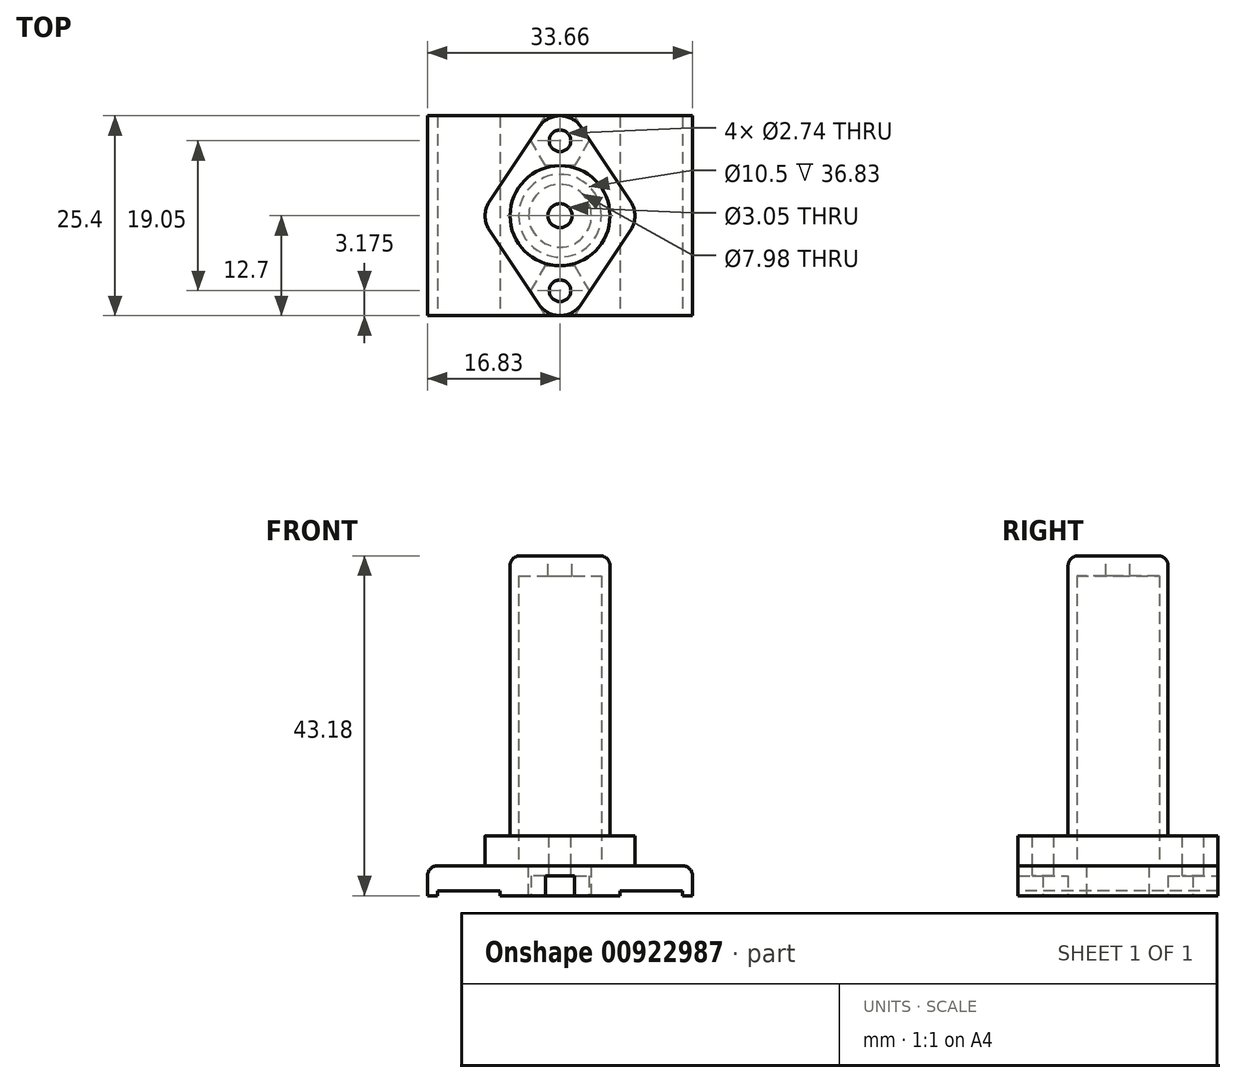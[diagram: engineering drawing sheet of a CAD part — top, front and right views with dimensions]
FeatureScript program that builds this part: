
annotation { "Feature Type Name" : "Feature", "Feature Type Description" : "" }
export const myFeature = defineFeature(function(context is Context, id is Id, definition is map)
    precondition{}
    {
        {
            var Q0;
            Q0=qCreatedBy(makeId("Top.planeOp"),FACE);
            var sketch = newSketch(context, id + "F0", { "sketchPlane" : qUnion([Q0])});
            skCircle(sketch, "E0", {"center": v(0, 0) * mm, "radius": 1.72 * mm});
            skCircle(sketch, "E1", {"center": v(0, 0) * mm, "radius": 2.54 * mm});
            skLineSegment(sketch, "E2", {"start": v(0, -2.54) * mm, "end": v(0, -12.7) * mm});
            skLineSegment(sketch, "E3", {"start": v(2.54, 0) * mm, "end": v(7.62, 0) * mm});
            skLineSegment(sketch, "E4", {"start": v(-2.54, 0) * mm, "end": v(-7.62, 0) * mm});
            skLineSegment(sketch, "E5", {"start": v(-7.62, 0) * mm, "end": v(-15.56, 0) * mm});
            skLineSegment(sketch, "E6", {"start": v(7.62, 0) * mm, "end": v(15.56, 0) * mm});
            skLineSegment(sketch, "E7.bottom", {"start": v(-7.62, 12.7) * mm, "end": v(-15.56, 12.7) * mm});
            skLineSegment(sketch, "E7.top", {"start": v(-7.62, -12.7) * mm, "end": v(-15.56, -12.7) * mm});
            skLineSegment(sketch, "E7.left", {"start": v(-7.62, 12.7) * mm, "end": v(-7.62, -12.7) * mm});
            skLineSegment(sketch, "E7.right", {"start": v(-15.56, 12.7) * mm, "end": v(-15.56, -12.7) * mm});
            skPoint(sketch, "E7.middle", {"position": v(-11.59, 0) * mm});
            skLineSegment(sketch, "E8.bottom", {"start": v(15.56, 12.7) * mm, "end": v(7.62, 12.7) * mm});
            skLineSegment(sketch, "E8.top", {"start": v(15.56, -12.7) * mm, "end": v(7.62, -12.7) * mm});
            skLineSegment(sketch, "E8.left", {"start": v(15.56, 12.7) * mm, "end": v(15.56, -12.7) * mm});
            skLineSegment(sketch, "E8.right", {"start": v(7.62, 12.7) * mm, "end": v(7.62, -12.7) * mm});
            skPoint(sketch, "E8.middle", {"position": v(11.59, 0) * mm});
            skPoint(sketch, "E8.cornerSnap0", {"position": v(-11.59, 12.7) * mm});
            skLineSegment(sketch, "E9.bottom", {"start": v(16.83, -12.7) * mm, "end": v(-16.83, -12.7) * mm});
            skLineSegment(sketch, "E9.top", {"start": v(16.83, 12.7) * mm, "end": v(-16.83, 12.7) * mm});
            skLineSegment(sketch, "E9.left", {"start": v(16.83, -12.7) * mm, "end": v(16.83, 12.7) * mm});
            skLineSegment(sketch, "E9.right", {"start": v(-16.83, -12.7) * mm, "end": v(-16.83, 12.7) * mm});
            skSolve(sketch);
        }
        {
            var Q0;
            {var subQ3=sQuery(id+"F0.wireOp",EDGE,"E9.right");Q0=makeQuery(id+"F0.imprint","IMPRINT",FACE,{"disambiguationData":[TD([[makeQuery(id+"F0.imprint","IMPRINT",EDGE,{"derivedFrom":subQ3}),-1.0]])]});}
            var Q1;
            {var subQ0=sQuery(id+"F0.wireOp",EDGE,"E5");Q1=makeQuery(id+"F0.imprint","IMPRINT",FACE,{"disambiguationData":[TD([[makeQuery(id+"F0.imprint","IMPRINT",EDGE,{"derivedFrom":subQ0}),-1.0]])]});}
            var Q2;
            {var subQ0=sQuery(id+"F0.wireOp",EDGE,"E5");Q2=makeQuery(id+"F0.imprint","IMPRINT",FACE,{"disambiguationData":[TD([[makeQuery(id+"F0.imprint","IMPRINT",EDGE,{"derivedFrom":subQ0}),1.0]])]});}
            var Q3;
            {var subQ4=sQuery(id+"F0.wireOp",EDGE,"E2");Q3=makeQuery(id+"F0.imprint","IMPRINT",FACE,{"disambiguationData":[TD([[makeQuery(id+"F0.imprint","IMPRINT",EDGE,{"derivedFrom":subQ4}),-1.0]])]});}
            var Q4;
            {var subQ4=sQuery(id+"F0.wireOp",EDGE,"E3");Q4=makeQuery(id+"F0.imprint","IMPRINT",FACE,{"disambiguationData":[TD([[makeQuery(id+"F0.imprint","IMPRINT",EDGE,{"derivedFrom":subQ4}),1.0]])]});}
            var Q5;
            {var subQ4=sQuery(id+"F0.wireOp",EDGE,"E2");Q5=makeQuery(id+"F0.imprint","IMPRINT",FACE,{"disambiguationData":[TD([[makeQuery(id+"F0.imprint","IMPRINT",EDGE,{"derivedFrom":subQ4}),1.0]])]});}
            var Q6;
            {var subQ0=sQuery(id+"F0.wireOp",EDGE,"E6");Q6=makeQuery(id+"F0.imprint","IMPRINT",FACE,{"disambiguationData":[TD([[makeQuery(id+"F0.imprint","IMPRINT",EDGE,{"derivedFrom":subQ0}),-1.0]])]});}
            var Q7;
            {var subQ0=sQuery(id+"F0.wireOp",EDGE,"E6");Q7=makeQuery(id+"F0.imprint","IMPRINT",FACE,{"disambiguationData":[TD([[makeQuery(id+"F0.imprint","IMPRINT",EDGE,{"derivedFrom":subQ0}),1.0]])]});}
            var Q8;
            {var subQ3=sQuery(id+"F0.wireOp",EDGE,"E9.left");Q8=makeQuery(id+"F0.imprint","IMPRINT",FACE,{"disambiguationData":[TD([[makeQuery(id+"F0.imprint","IMPRINT",EDGE,{"derivedFrom":subQ3}),1.0]])]});}
            extrude(context, id + "F1", {"entities" : qUnion([Q0, Q1, Q2, Q3, Q4, Q5, Q6, Q7, Q8]), "depth" : 3.8 * mm, "offsetDistance" : 25.4 * mm});
        }
        {
            var Q0;
            {var subQ0=sQuery(id+"F0.wireOp",EDGE,"E5");Q0=makeQuery(id+"F0.imprint","IMPRINT",FACE,{"disambiguationData":[TD([[makeQuery(id+"F0.imprint","IMPRINT",EDGE,{"derivedFrom":subQ0}),1.0]])]});}
            var Q1;
            {var subQ0=sQuery(id+"F0.wireOp",EDGE,"E5");Q1=makeQuery(id+"F0.imprint","IMPRINT",FACE,{"disambiguationData":[TD([[makeQuery(id+"F0.imprint","IMPRINT",EDGE,{"derivedFrom":subQ0}),-1.0]])]});}
            var Q2;
            {var subQ0=sQuery(id+"F0.wireOp",EDGE,"E6");Q2=makeQuery(id+"F0.imprint","IMPRINT",FACE,{"disambiguationData":[TD([[makeQuery(id+"F0.imprint","IMPRINT",EDGE,{"derivedFrom":subQ0}),1.0]])]});}
            var Q3;
            {var subQ0=sQuery(id+"F0.wireOp",EDGE,"E6");Q3=makeQuery(id+"F0.imprint","IMPRINT",FACE,{"disambiguationData":[TD([[makeQuery(id+"F0.imprint","IMPRINT",EDGE,{"derivedFrom":subQ0}),-1.0]])]});}
            extrude(context, id + "F2", {"entities" : qUnion([Q0, Q1, Q2, Q3]), "operationType" : NewBodyOperationType.REMOVE, "depth" : 0.64 * mm, "offsetDistance" : 25.4 * mm});
        }
        {
            var Q0;
            Q0=makeQuery(id+"F1.opExtrude","CAP_FACE",FACE,{"disambiguationData":[OSD([sQuery(id+"F0.wireOp",EDGE,"E1"),sQuery(id+"F0.wireOp",EDGE,"E7.bottom"),sQuery(id+"F0.wireOp",EDGE,"E7.top"),sQuery(id+"F0.wireOp",EDGE,"E8.bottom"),sQuery(id+"F0.wireOp",EDGE,"E8.top"),sQuery(id+"F0.wireOp",EDGE,"E9.bottom"),sQuery(id+"F0.wireOp",EDGE,"E9.top"),sQuery(id+"F0.wireOp",EDGE,"E9.left"),sQuery(id+"F0.wireOp",EDGE,"E9.right")])],"isStart":false});
            var sketch = newSketch(context, id + "F3", { "sketchPlane" : qUnion([Q0])});
            skCircle(sketch, "E10", {"center": v(0, 0) * mm, "radius": 3.99 * mm});
            skSolve(sketch);
        }
        {
            var Q0;
            Q0=makeQuery(id+"F3.imprint","IMPRINT",FACE,{"disambiguationData":[TD([[makeQuery(id+"F3.imprint","IMPRINT",EDGE,{"derivedFrom":sQuery(id+"F3.wireOp",EDGE,"E10")}),1.0]])]});
            extrude(context, id + "F4", {"entities" : qUnion([Q0]), "operationType" : NewBodyOperationType.REMOVE, "endBound" : BoundingType.UP_TO_NEXT, "oppositeDirection" : true, "depth" : 2.08 * mm, "offsetDistance" : 25.4 * mm});
        }
        {
            var Q0;
            Q0=makeQuery(id+"F3.imprint","IMPRINT",FACE,{"disambiguationData":[TD([[makeQuery(id+"F3.imprint","IMPRINT",EDGE,{"derivedFrom":sQuery(id+"F3.wireOp",EDGE,"E10")}),-1.0]])]});
            var sketch = newSketch(context, id + "F5", { "sketchPlane" : qUnion([Q0])});
            skLineSegment(sketch, "E11", {"start": v(0, 0) * mm, "end": v(0, 12.7) * mm});
            skLineSegment(sketch, "E12", {"start": v(0, 0) * mm, "end": v(0, -12.7) * mm});
            skLineSegment(sketch, "E13", {"start": v(0, 12.7) * mm, "end": v(0, 9.52) * mm});
            skLineSegment(sketch, "E14", {"start": v(0, -12.7) * mm, "end": v(0, -9.53) * mm});
            skCircle(sketch, "E15", {"center": v(0, 9.52) * mm, "radius": 1.37 * mm});
            skCircle(sketch, "E16", {"center": v(0, -9.53) * mm, "radius": 1.37 * mm});
            skSolve(sketch);
        }
        {
            var Q0;
            Q0 = qSketchRegion(id + "F5", true);
            extrude(context, id + "F6", {"entities" : qUnion([Q0]), "operationType" : NewBodyOperationType.REMOVE, "endBound" : BoundingType.UP_TO_NEXT, "oppositeDirection" : true, "depth" : 25.4 * mm, "offsetDistance" : 25.4 * mm});
        }
        {
            var Q0;
            {var subQ4=sQuery(id+"F0.wireOp",EDGE,"E2");Q0=makeQuery(id+"F0.imprint","IMPRINT",FACE,{"disambiguationData":[TD([[makeQuery(id+"F0.imprint","IMPRINT",EDGE,{"derivedFrom":subQ4}),-1.0]])]});}
            var sketch = newSketch(context, id + "F7", { "sketchPlane" : qUnion([Q0])});
            skLineSegment(sketch, "E17", {"start": v(0, 0) * mm, "end": v(0, -9.53) * mm});
            skLineSegment(sketch, "E18", {"start": v(0, 0) * mm, "end": v(0, 9.53) * mm});
            skLineSegment(sketch, "E19", {"start": v(0, -9.53) * mm, "end": v(-5.62, -9.53) * mm});
            skLineSegment(sketch, "E20", {"start": v(0, 9.53) * mm, "end": v(-5.88, 9.53) * mm});
            skCircle(sketch, "E21.cCircle", {"center": v(0, -9.53) * mm, "radius": 3.18 * mm, "construction": true});
            skLineSegment(sketch, "E21.0", {"start": v(1.83, -12.7) * mm, "end": v(-1.83, -12.7) * mm});
            skLineSegment(sketch, "E21.1", {"start": v(-1.83, -12.7) * mm, "end": v(-3.67, -9.53) * mm});
            skLineSegment(sketch, "E21.2", {"start": v(-3.67, -9.52) * mm, "end": v(-1.83, -6.35) * mm});
            skLineSegment(sketch, "E21.3", {"start": v(-1.83, -6.35) * mm, "end": v(1.83, -6.35) * mm});
            skLineSegment(sketch, "E21.4", {"start": v(1.83, -6.35) * mm, "end": v(3.67, -9.53) * mm});
            skLineSegment(sketch, "E21.5", {"start": v(3.67, -9.53) * mm, "end": v(1.83, -12.7) * mm});
            skPoint(sketch, "E21.0.midPoint", {"position": v(0, -12.7) * mm});
            skCircle(sketch, "E22.cCircle", {"center": v(0, 9.53) * mm, "radius": 3.18 * mm, "construction": true});
            skLineSegment(sketch, "E22.0", {"start": v(1.83, 6.35) * mm, "end": v(-1.83, 6.35) * mm});
            skLineSegment(sketch, "E22.1", {"start": v(-1.83, 6.35) * mm, "end": v(-3.67, 9.52) * mm});
            skLineSegment(sketch, "E22.2", {"start": v(-3.67, 9.52) * mm, "end": v(-1.83, 12.7) * mm});
            skLineSegment(sketch, "E22.3", {"start": v(-1.83, 12.7) * mm, "end": v(1.83, 12.7) * mm});
            skLineSegment(sketch, "E22.4", {"start": v(1.83, 12.7) * mm, "end": v(3.67, 9.53) * mm});
            skLineSegment(sketch, "E22.5", {"start": v(3.67, 9.53) * mm, "end": v(1.83, 6.35) * mm});
            skPoint(sketch, "E22.0.midPoint", {"position": v(0, 6.35) * mm});
            skSolve(sketch);
        }
        {
            var Q0;
            {var subQ0=sQuery(id+"F7.wireOp",EDGE,"E21.4");Q0=makeQuery(id+"F7.imprint","IMPRINT",FACE,{"disambiguationData":[TD([[makeQuery(id+"F7.imprint","IMPRINT",EDGE,{"derivedFrom":subQ0}),-1.0]])]});}
            var Q1;
            {var subQ4=sQuery(id+"F7.wireOp",EDGE,"E21.1");Q1=makeQuery(id+"F7.imprint","IMPRINT",FACE,{"disambiguationData":[TD([[makeQuery(id+"F7.imprint","IMPRINT",EDGE,{"derivedFrom":subQ4}),-1.0]])]});}
            var Q2;
            {var subQ5=sQuery(id+"F7.wireOp",EDGE,"E21.2");Q2=makeQuery(id+"F7.imprint","IMPRINT",FACE,{"disambiguationData":[TD([[makeQuery(id+"F7.imprint","IMPRINT",EDGE,{"derivedFrom":subQ5}),-1.0]])]});}
            var Q3;
            {var subQ0=sQuery(id+"F7.wireOp",EDGE,"E22.2");Q3=makeQuery(id+"F7.imprint","IMPRINT",FACE,{"disambiguationData":[TD([[makeQuery(id+"F7.imprint","IMPRINT",EDGE,{"derivedFrom":subQ0}),-1.0]])]});}
            var Q4;
            {var subQ5=sQuery(id+"F7.wireOp",EDGE,"E22.1");Q4=makeQuery(id+"F7.imprint","IMPRINT",FACE,{"disambiguationData":[TD([[makeQuery(id+"F7.imprint","IMPRINT",EDGE,{"derivedFrom":subQ5}),-1.0]])]});}
            extrude(context, id + "F8", {"entities" : qUnion([Q0, Q1, Q2, Q3, Q4]), "operationType" : NewBodyOperationType.REMOVE, "depth" : 2.54 * mm, "offsetDistance" : 25.4 * mm});
        }
        {
            var Q0;
            Q0=qCreatedBy(makeId("Right.planeOp"),FACE);
            var sketch = newSketch(context, id + "F9", { "sketchPlane" : qUnion([Q0])});
            skLineSegment(sketch, "E23", {"start": v(0, 0) * mm, "end": v(0, 7.62) * mm});
            skLineSegment(sketch, "E24", {"start": v(0, 7.62) * mm, "end": v(0, 3.81) * mm});
            skLineSegment(sketch, "E25.bottom", {"start": v(-12.7, 7.62) * mm, "end": v(12.7, 7.62) * mm});
            skLineSegment(sketch, "E25.top", {"start": v(-12.7, 3.81) * mm, "end": v(12.7, 3.81) * mm});
            skLineSegment(sketch, "E25.left", {"start": v(-12.7, 7.62) * mm, "end": v(-12.7, 3.8) * mm});
            skLineSegment(sketch, "E25.right", {"start": v(12.7, 7.62) * mm, "end": v(12.7, 3.8) * mm});
            skPoint(sketch, "E25.middle", {"position": v(0, 5.71) * mm});
            skSolve(sketch);
        }
        {
            var Q0;
            {var subQ5=sQuery(id+"F9.wireOp",EDGE,"E25.right");Q0=makeQuery(id+"F9.imprint","IMPRINT",FACE,{"disambiguationData":[TD([[makeQuery(id+"F9.imprint","IMPRINT",EDGE,{"derivedFrom":subQ5}),-1.0]])]});}
            var Q1;
            {var subQ5=sQuery(id+"F9.wireOp",EDGE,"E25.left");Q1=makeQuery(id+"F9.imprint","IMPRINT",FACE,{"disambiguationData":[TD([[makeQuery(id+"F9.imprint","IMPRINT",EDGE,{"derivedFrom":subQ5}),1.0]])]});}
            extrude(context, id + "F10", {"entities" : qUnion([Q0, Q1]), "endBound" : BoundingType.SYMMETRIC, "depth" : 19.05 * mm, "offsetDistance" : 25.4 * mm});
        }
        {
            var Q0;
            Q0=makeQuery(id+"F10.opExtrude","SWEPT_FACE",FACE,{"disambiguationData":[OSD([sQuery(id+"F9.wireOp",EDGE,"E25.bottom")])]});
            var sketch = newSketch(context, id + "F11", { "sketchPlane" : qUnion([Q0])});
            skLineSegment(sketch, "E26", {"start": v(0, 12.7) * mm, "end": v(0, 9.53) * mm});
            skLineSegment(sketch, "E27", {"start": v(0, -12.7) * mm, "end": v(0, -9.53) * mm});
            skCircle(sketch, "E28", {"center": v(0, 9.53) * mm, "radius": 1.37 * mm});
            skCircle(sketch, "E29", {"center": v(0, -9.53) * mm, "radius": 1.37 * mm});
            skSolve(sketch);
        }
        {
            var Q0;
            Q0=makeQuery(id+"F11.imprint","IMPRINT",FACE,{"disambiguationData":[TD([[makeQuery(id+"F11.imprint","IMPRINT",EDGE,{"derivedFrom":sQuery(id+"F11.wireOp",EDGE,"E28")}),1.0]])]});
            var Q1;
            Q1=makeQuery(id+"F11.imprint","IMPRINT",FACE,{"disambiguationData":[TD([[makeQuery(id+"F11.imprint","IMPRINT",EDGE,{"derivedFrom":sQuery(id+"F11.wireOp",EDGE,"E29")}),1.0]])]});
            extrude(context, id + "F12", {"entities" : qUnion([Q0, Q1]), "operationType" : NewBodyOperationType.REMOVE, "oppositeDirection" : true, "depth" : 3.8 * mm, "offsetDistance" : 25.4 * mm});
        }
        {
            var Q0;
            Q0=makeQuery(id+"F10.opExtrude","SWEPT_FACE",FACE,{"disambiguationData":[OSD([sQuery(id+"F9.wireOp",EDGE,"E25.bottom")])]});
            var sketch = newSketch(context, id + "F13", { "sketchPlane" : qUnion([Q0])});
            skCircle(sketch, "E30", {"center": v(0, 9.53) * mm, "radius": 3.18 * mm});
            skCircle(sketch, "E31", {"center": v(0, -9.53) * mm, "radius": 3.18 * mm});
            skLineSegment(sketch, "E32", {"start": v(-9.53, 0) * mm, "end": v(-6.35, 0) * mm});
            skLineSegment(sketch, "E33", {"start": v(9.53, 0) * mm, "end": v(6.35, 0) * mm});
            skCircle(sketch, "E34", {"center": v(-6.35, 0) * mm, "radius": 3.18 * mm});
            skCircle(sketch, "E35", {"center": v(6.35, 0) * mm, "radius": 3.18 * mm});
            skLineSegment(sketch, "E36", {"start": v(-9, 1.76) * mm, "end": v(-2.64, 11.29) * mm});
            skLineSegment(sketch, "E37", {"start": v(2.64, 11.29) * mm, "end": v(9, 1.76) * mm});
            skLineSegment(sketch, "E38", {"start": v(-9, -1.76) * mm, "end": v(-2.64, -11.29) * mm});
            skLineSegment(sketch, "E39", {"start": v(2.64, -11.29) * mm, "end": v(9, -1.76) * mm});
            skSolve(sketch);
        }
        {
            var Q0;
            {var subQ6=sQuery(id+"F13.wireOp",EDGE,"E36");Q0=makeQuery(id+"F13.imprint","IMPRINT",FACE,{"disambiguationData":[TD([[makeQuery(id+"F13.imprint","IMPRINT",EDGE,{"derivedFrom":subQ6}),1.0]])]});}
            var Q1;
            {var subQ6=sQuery(id+"F13.wireOp",EDGE,"E37");Q1=makeQuery(id+"F13.imprint","IMPRINT",FACE,{"disambiguationData":[TD([[makeQuery(id+"F13.imprint","IMPRINT",EDGE,{"derivedFrom":subQ6}),1.0]])]});}
            var Q2;
            {var subQ0=sQuery(id+"F13.wireOp",EDGE,"E38");Q2=makeQuery(id+"F13.imprint","IMPRINT",FACE,{"disambiguationData":[TD([[makeQuery(id+"F13.imprint","IMPRINT",EDGE,{"derivedFrom":subQ0}),-1.0]])]});}
            var Q3;
            {var subQ0=sQuery(id+"F13.wireOp",EDGE,"E39");Q3=makeQuery(id+"F13.imprint","IMPRINT",FACE,{"disambiguationData":[TD([[makeQuery(id+"F13.imprint","IMPRINT",EDGE,{"derivedFrom":subQ0}),-1.0]])]});}
            extrude(context, id + "F14", {"entities" : qUnion([Q0, Q1, Q2, Q3]), "operationType" : NewBodyOperationType.REMOVE, "oppositeDirection" : true, "depth" : 3.8 * mm, "offsetDistance" : 25.4 * mm});
        }
        {
            var Q0;
            {var subQ0=sQuery(id+"F13.wireOp",EDGE,"E36");Q0=makeQuery(id+"F13.imprint","IMPRINT",FACE,{"disambiguationData":[TD([[makeQuery(id+"F13.imprint","IMPRINT",EDGE,{"derivedFrom":subQ0}),-1.0]])]});}
            var sketch = newSketch(context, id + "F15", { "sketchPlane" : qUnion([Q0])});
            skCircle(sketch, "E40", {"center": v(0, 0) * mm, "radius": 6.35 * mm});
            skLineSegment(sketch, "E41", {"start": v(0, 0) * mm, "end": v(0, 9.53) * mm});
            skLineSegment(sketch, "E42", {"start": v(0, 0) * mm, "end": v(0, -9.53) * mm});
            skCircle(sketch, "E43", {"center": v(0, 9.53) * mm, "radius": 2.54 * mm});
            skCircle(sketch, "E44", {"center": v(0, -9.53) * mm, "radius": 2.54 * mm});
            skSolve(sketch);
        }
        {
            var Q0;
            {var subQ0=sQuery(id+"F15.wireOp",EDGE,"E40");var subQ1=sQuery(id+"F13.wireOp",EDGE,"E34");var subQ2=makeQuery(id+"F13.imprint","IMPRINT",EDGE,{"disambiguationData":[TD([[makeQuery(id+"F13.imprint","INTERSECT",VERTEX,{"derivedFrom":[subQ1,sQuery(id+"F13.wireOp",EDGE,"E36")]}),1.0]])],"derivedFrom":subQ1});var subQ3=makeQuery(id+"F15.imprint","INTERSECT",VERTEX,{"disambiguationData":[OD(0.0)],"derivedFrom":[subQ2,subQ0]});Q0=makeQuery(id+"F15.imprint","IMPRINT",FACE,{"disambiguationData":[TD([[makeQuery(id+"F15.imprint","IMPRINT",EDGE,{"disambiguationData":[TD([[subQ3,-1.0]])],"derivedFrom":subQ0}),1.0]])]});}
            var Q1;
            {var subQ0=sQuery(id+"F15.wireOp",EDGE,"E42");var subQ1=sQuery(id+"F15.wireOp",EDGE,"E41");var subQ2=makeQuery(id+"F15.imprint","INTERSECT",VERTEX,{"derivedFrom":[subQ1,subQ0]});Q1=makeQuery(id+"F15.imprint","IMPRINT",FACE,{"disambiguationData":[TD([[makeQuery(id+"F15.imprint","IMPRINT",EDGE,{"disambiguationData":[TD([[subQ2,-1.0]])],"derivedFrom":subQ1}),1.0]])]});}
            var Q2;
            {var subQ0=sQuery(id+"F15.wireOp",EDGE,"E42");var subQ1=sQuery(id+"F15.wireOp",EDGE,"E41");var subQ2=makeQuery(id+"F15.imprint","INTERSECT",VERTEX,{"derivedFrom":[subQ1,subQ0]});Q2=makeQuery(id+"F15.imprint","IMPRINT",FACE,{"disambiguationData":[TD([[makeQuery(id+"F15.imprint","IMPRINT",EDGE,{"disambiguationData":[TD([[subQ2,-1.0]])],"derivedFrom":subQ1}),-1.0]])]});}
            var Q3;
            {var subQ0=sQuery(id+"F15.wireOp",EDGE,"E40");var subQ1=sQuery(id+"F13.wireOp",EDGE,"E35");var subQ2=makeQuery(id+"F13.imprint","IMPRINT",EDGE,{"disambiguationData":[TD([[makeQuery(id+"F13.imprint","INTERSECT",VERTEX,{"derivedFrom":[subQ1,sQuery(id+"F13.wireOp",EDGE,"E37")]}),-1.0]])],"derivedFrom":subQ1});var subQ3=makeQuery(id+"F15.imprint","INTERSECT",VERTEX,{"disambiguationData":[OD(0.0)],"derivedFrom":[subQ2,subQ0]});Q3=makeQuery(id+"F15.imprint","IMPRINT",FACE,{"disambiguationData":[TD([[makeQuery(id+"F15.imprint","IMPRINT",EDGE,{"disambiguationData":[TD([[subQ3,1.0]])],"derivedFrom":subQ0}),1.0]])]});}
            extrude(context, id + "F16", {"entities" : qUnion([Q0, Q1, Q2, Q3]), "operationType" : NewBodyOperationType.ADD, "depth" : 35.56 * mm, "offsetDistance" : 25.4 * mm});
        }
        {
            var Q0;
            Q0=makeQuery(id+"F14.boolean.opBoolean","COPY",EDGE,{"derivedFrom":makeQuery(id+"F14.opExtrude","CAP_EDGE",EDGE,{"disambiguationData":[OSD([sQuery(id+"F13.wireOp",EDGE,"E39")])],"isStart":true})});
            var Q1;
            Q1=makeQuery(id+"F1.opExtrude","CAP_EDGE",EDGE,{"disambiguationData":[OSD([sQuery(id+"F0.wireOp",EDGE,"E9.left")])],"isStart":false});
            var Q2;
            Q2=makeQuery(id+"F1.opExtrude","CAP_EDGE",EDGE,{"disambiguationData":[OSD([sQuery(id+"F0.wireOp",EDGE,"E9.right")])],"isStart":false});
            fillet(context, id + "F17", {"entities" : qUnion([Q0, Q1, Q2]), "radius" : 1.27 * mm, "tangentPropagation" : true, "allowEdgeOverflow" : false});
        }
        {
            var Q0;
            Q0=makeQuery(id+"F10.opExtrude","SWEPT_FACE",FACE,{"disambiguationData":[OSD([sQuery(id+"F9.wireOp",EDGE,"E25.top")])]});
            var sketch = newSketch(context, id + "F18", { "sketchPlane" : qUnion([Q0])});
            skCircle(sketch, "E45", {"center": v(0, 0) * mm, "radius": 5.25 * mm});
            skSolve(sketch);
        }
        {
            var Q0;
            Q0=makeQuery(id+"F18.imprint","IMPRINT",FACE,{"disambiguationData":[TD([[makeQuery(id+"F18.imprint","IMPRINT",EDGE,{"derivedFrom":sQuery(id+"F18.wireOp",EDGE,"E45")}),1.0]])]});
            extrude(context, id + "F19", {"entities" : qUnion([Q0]), "operationType" : NewBodyOperationType.REMOVE, "oppositeDirection" : true, "depth" : 36.83 * mm, "offsetDistance" : 25.4 * mm});
        }
        {
            var Q0;
            Q0=makeQuery(id+"F16.opExtrude","CAP_FACE",FACE,{"disambiguationData":[OSD([sQuery(id+"F15.wireOp",EDGE,"E40")])],"isStart":false});
            var sketch = newSketch(context, id + "F20", { "sketchPlane" : qUnion([Q0])});
            skCircle(sketch, "E46", {"center": v(0, 0) * mm, "radius": 1.52 * mm});
            skSolve(sketch);
        }
        {
            var Q0;
            Q0=makeQuery(id+"F20.imprint","IMPRINT",FACE,{"disambiguationData":[TD([[makeQuery(id+"F20.imprint","IMPRINT",EDGE,{"derivedFrom":sQuery(id+"F20.wireOp",EDGE,"E46")}),1.0]])]});
            extrude(context, id + "F21", {"entities" : qUnion([Q0]), "operationType" : NewBodyOperationType.REMOVE, "oppositeDirection" : true, "depth" : 25.4 * mm, "offsetDistance" : 25.4 * mm});
        }
        {
            var Q0;
            Q0=makeQuery(id+"F16.opExtrude","CAP_EDGE",EDGE,{"disambiguationData":[OSD([sQuery(id+"F15.wireOp",EDGE,"E40")])],"isStart":false});
            fillet(context, id + "F22", {"entities" : qUnion([Q0]), "radius" : 1.27 * mm, "tangentPropagation" : true, "allowEdgeOverflow" : false});
        }
    });
